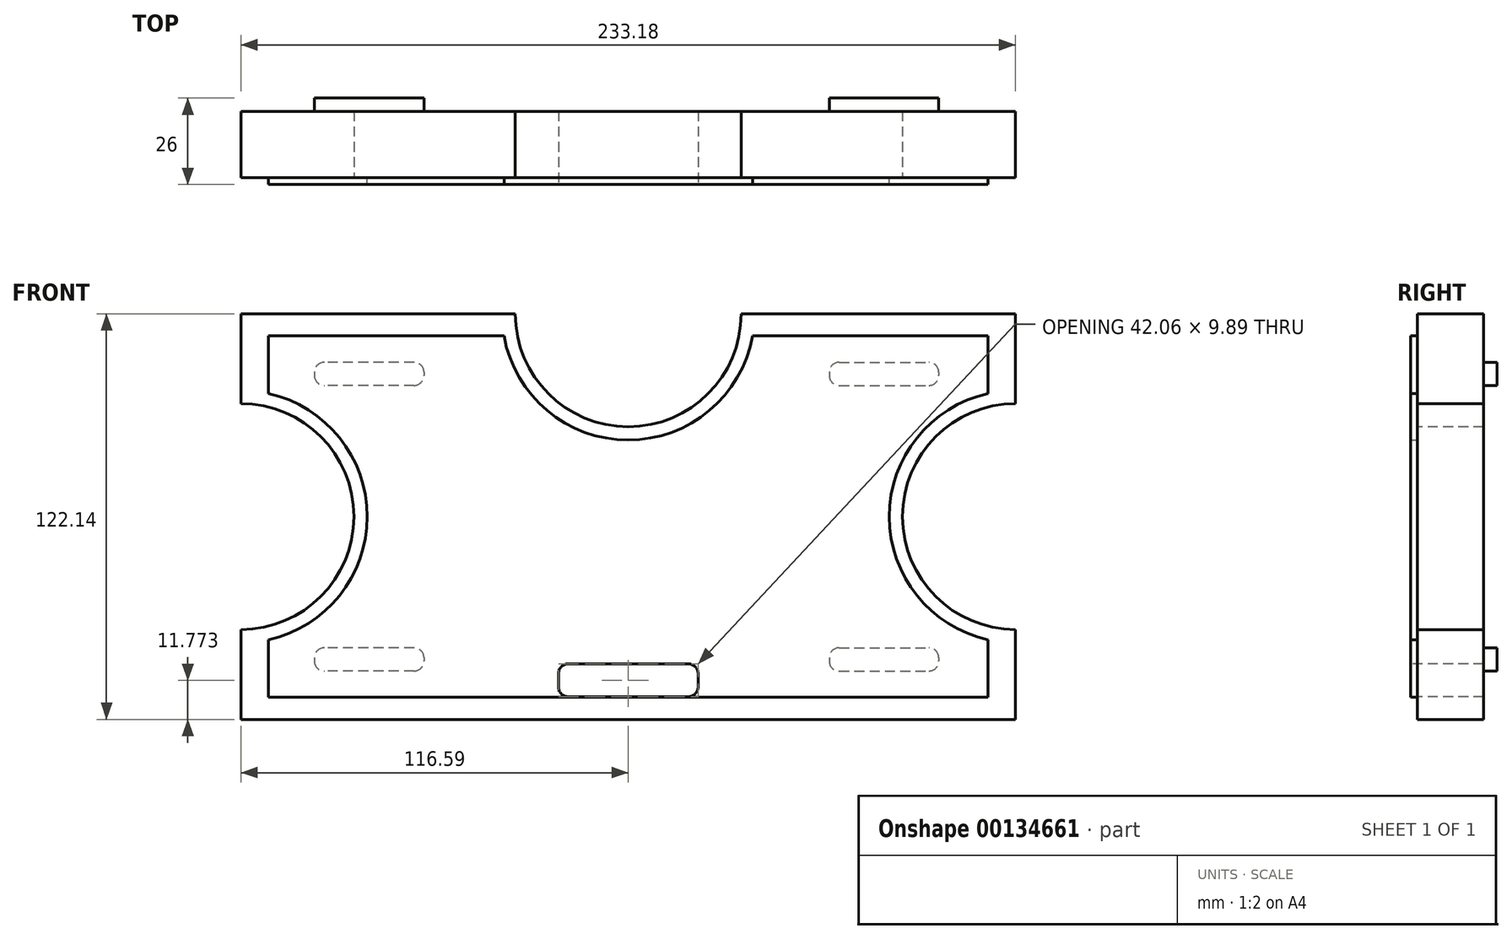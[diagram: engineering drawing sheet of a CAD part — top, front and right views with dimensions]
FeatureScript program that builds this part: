
annotation { "Feature Type Name" : "Feature", "Feature Type Description" : "" }
export const myFeature = defineFeature(function(context is Context, id is Id, definition is map)
    precondition{}
    {
        {
            var Q0;
            Q0=qCreatedBy(makeId("Front.planeOp"),FACE);
            var sketch = newSketch(context, id + "F0", { "sketchPlane" : qUnion([Q0])});
            skLineSegment(sketch, "E0.bottom", {"start": v(116.6, 61.07) * mm, "end": v(34, 61.07) * mm});
            skLineSegment(sketch, "E0.top", {"start": v(116.6, -61.07) * mm, "end": v(34, -61.07) * mm});
            skLineSegment(sketch, "E0.left", {"start": v(116.6, 61.07) * mm, "end": v(116.6, 34) * mm});
            skLineSegment(sketch, "E0.right", {"start": v(-116.6, 61.07) * mm, "end": v(-116.6, 34) * mm});
            skPoint(sketch, "E0.middle", {"position": v(0, 0) * mm});
            skArc(sketch, "E1", {"start": v(-34, 61.07) * mm, "mid": v(0, 27.07) * mm, "end": v(34, 61.07) * mm});
            skArc(sketch, "E2", {"start": v(116.6, 34) * mm, "mid": v(82.6, 0) * mm, "end": v(116.6, -34) * mm});
            skArc(sketch, "E3", {"start": v(-116.6, -34) * mm, "mid": v(-82.6, 0) * mm, "end": v(-116.6, 34) * mm});
            skLineSegment(sketch, "E4.trimOffspring", {"start": v(-116.6, -34) * mm, "end": v(-116.6, -61.07) * mm});
            skLineSegment(sketch, "E5.trimOffspring", {"start": v(34, -61.07) * mm, "end": v(-116.6, -61.07) * mm});
            skLineSegment(sketch, "E6.trimOffspring", {"start": v(-34, 61.07) * mm, "end": v(-116.6, 61.07) * mm});
            skLineSegment(sketch, "E7.trimOffspring", {"start": v(116.6, -34) * mm, "end": v(116.6, -61.07) * mm});
            skLineSegment(sketch, "E8.bottom", {"start": v(18.03, -44.35) * mm, "end": v(-18.03, -44.35) * mm});
            skLineSegment(sketch, "E8.top", {"start": v(18.03, -54.24) * mm, "end": v(-18.03, -54.24) * mm});
            skLineSegment(sketch, "E8.left", {"start": v(21.03, -47.35) * mm, "end": v(21.03, -51.24) * mm});
            skLineSegment(sketch, "E8.right", {"start": v(-21.03, -47.35) * mm, "end": v(-21.03, -51.24) * mm});
            skPoint(sketch, "E8.middle", {"position": v(0, -49.3) * mm});
            skPoint(sketch, "E9.visualSharp", {"position": v(-21.03, -44.35) * mm});
            skArc(sketch, "E9.filletArc", {"start": v(-18.03, -44.35) * mm, "mid": v(-20.15, -45.23) * mm, "end": v(-21.03, -47.35) * mm});
            skPoint(sketch, "E10.visualSharp", {"position": v(21.03, -44.35) * mm});
            skArc(sketch, "E10.filletArc", {"start": v(21.03, -47.35) * mm, "mid": v(20.15, -45.23) * mm, "end": v(18.03, -44.35) * mm});
            skPoint(sketch, "E11.visualSharp", {"position": v(21.03, -54.24) * mm});
            skArc(sketch, "E11.filletArc", {"start": v(18.03, -54.24) * mm, "mid": v(20.15, -53.36) * mm, "end": v(21.03, -51.24) * mm});
            skPoint(sketch, "E12.visualSharp", {"position": v(-21.03, -54.24) * mm});
            skArc(sketch, "E12.filletArc", {"start": v(-21.03, -51.24) * mm, "mid": v(-20.15, -53.36) * mm, "end": v(-18.03, -54.24) * mm});
            skSolve(sketch);
        }
        {
            var Q0;
            Q0=makeQuery(id+"F0.imprint","IMPRINT",FACE,{"disambiguationData":[TD([[makeQuery(id+"F0.imprint","IMPRINT",EDGE,{"derivedFrom":sQuery(id+"F0.wireOp",EDGE,"E0.bottom")}),1.0]])]});
            extrude(context, id + "F1", {"entities" : qUnion([Q0]), "oppositeDirection" : true, "depth" : 20 * mm});
        }
        {
            var Q0;
            Q0=makeQuery(id+"F1.opExtrude","CAP_FACE",FACE,{"disambiguationData":[OSD([sQuery(id+"F0.wireOp",EDGE,"E0.bottom"),sQuery(id+"F0.wireOp",EDGE,"E0.top"),sQuery(id+"F0.wireOp",EDGE,"E0.left"),sQuery(id+"F0.wireOp",EDGE,"E0.right"),sQuery(id+"F0.wireOp",EDGE,"E1"),sQuery(id+"F0.wireOp",EDGE,"E2"),sQuery(id+"F0.wireOp",EDGE,"E3"),sQuery(id+"F0.wireOp",EDGE,"E4.trimOffspring"),sQuery(id+"F0.wireOp",EDGE,"E5.trimOffspring"),sQuery(id+"F0.wireOp",EDGE,"E6.trimOffspring"),sQuery(id+"F0.wireOp",EDGE,"E7.trimOffspring"),sQuery(id+"F0.wireOp",EDGE,"E8.bottom"),sQuery(id+"F0.wireOp",EDGE,"E8.top"),sQuery(id+"F0.wireOp",EDGE,"E8.left"),sQuery(id+"F0.wireOp",EDGE,"E8.right")])],"isStart":true});
            var sketch = newSketch(context, id + "F2", { "sketchPlane" : qUnion([Q0])});
            skLineSegment(sketch, "E13.bottom", {"start": v(108.3, 54.4) * mm, "end": v(37.41, 54.4) * mm});
            skLineSegment(sketch, "E13.top", {"start": v(108.3, -54.4) * mm, "end": v(-108.3, -54.4) * mm});
            skLineSegment(sketch, "E13.left", {"start": v(108.3, 54.4) * mm, "end": v(108.3, 37.08) * mm});
            skLineSegment(sketch, "E13.right", {"start": v(-108.3, 54.4) * mm, "end": v(-108.3, 37.08) * mm});
            skPoint(sketch, "E13.middle", {"position": v(0, 0) * mm});
            skArc(sketch, "E14", {"start": v(-108.3, -37.08) * mm, "mid": v(-78.6, 0) * mm, "end": v(-108.3, 37.08) * mm});
            skArc(sketch, "E15", {"start": v(108.3, 37.08) * mm, "mid": v(78.6, 0) * mm, "end": v(108.3, -37.08) * mm});
            skLineSegment(sketch, "E16.trimOffspring", {"start": v(-108.3, -37.08) * mm, "end": v(-108.3, -54.4) * mm});
            skLineSegment(sketch, "E17.trimOffspring", {"start": v(108.3, -37.08) * mm, "end": v(108.3, -54.4) * mm});
            skArc(sketch, "E18", {"start": v(-37.41, 54.4) * mm, "mid": v(0, 23.07) * mm, "end": v(37.41, 54.4) * mm});
            skLineSegment(sketch, "E19.trimOffspring", {"start": v(-37.41, 54.4) * mm, "end": v(-108.3, 54.4) * mm});
            skSolve(sketch);
        }
        {
            var Q0;
            Q0=makeQuery(id+"F2.imprint","IMPRINT",FACE,{"disambiguationData":[TD([[makeQuery(id+"F2.imprint","IMPRINT",EDGE,{"derivedFrom":sQuery(id+"F2.wireOp",EDGE,"E13.bottom")}),1.0]])]});
            extrude(context, id + "F3", {"entities" : qUnion([Q0]), "operationType" : NewBodyOperationType.ADD, "depth" : 2 * mm});
        }
        {
            var Q0;
            Q0=makeQuery(id+"F1.opExtrude","CAP_FACE",FACE,{"disambiguationData":[OSD([sQuery(id+"F0.wireOp",EDGE,"E0.bottom"),sQuery(id+"F0.wireOp",EDGE,"E0.top"),sQuery(id+"F0.wireOp",EDGE,"E0.left"),sQuery(id+"F0.wireOp",EDGE,"E0.right"),sQuery(id+"F0.wireOp",EDGE,"E1"),sQuery(id+"F0.wireOp",EDGE,"E2"),sQuery(id+"F0.wireOp",EDGE,"E3"),sQuery(id+"F0.wireOp",EDGE,"E4.trimOffspring"),sQuery(id+"F0.wireOp",EDGE,"E5.trimOffspring"),sQuery(id+"F0.wireOp",EDGE,"E6.trimOffspring"),sQuery(id+"F0.wireOp",EDGE,"E7.trimOffspring"),sQuery(id+"F0.wireOp",EDGE,"E8.bottom"),sQuery(id+"F0.wireOp",EDGE,"E8.top"),sQuery(id+"F0.wireOp",EDGE,"E8.left"),sQuery(id+"F0.wireOp",EDGE,"E8.right")])],"isStart":false});
            var sketch = newSketch(context, id + "F4", { "sketchPlane" : qUnion([Q0])});
            skLineSegment(sketch, "E20.bottom", {"start": v(-63.5, 46.5) * mm, "end": v(-90.5, 46.5) * mm});
            skLineSegment(sketch, "E20.top", {"start": v(-63.5, 39.5) * mm, "end": v(-90.5, 39.5) * mm});
            skLineSegment(sketch, "E20.left", {"start": v(-60.5, 43.5) * mm, "end": v(-60.5, 42.5) * mm});
            skLineSegment(sketch, "E20.right", {"start": v(-93.5, 43.5) * mm, "end": v(-93.5, 42.5) * mm});
            skPoint(sketch, "E20.middle", {"position": v(-77, 43) * mm});
            skLineSegment(sketch, "E21.bottom", {"start": v(-63.5, -39.5) * mm, "end": v(-90.5, -39.5) * mm});
            skLineSegment(sketch, "E21.top", {"start": v(-63.5, -46.5) * mm, "end": v(-90.5, -46.5) * mm});
            skLineSegment(sketch, "E21.left", {"start": v(-60.5, -42.5) * mm, "end": v(-60.5, -43.5) * mm});
            skLineSegment(sketch, "E21.right", {"start": v(-93.5, -42.5) * mm, "end": v(-93.5, -43.5) * mm});
            skPoint(sketch, "E21.middle", {"position": v(-77, -43) * mm});
            skLineSegment(sketch, "E22.bottom", {"start": v(64.5, 46.5) * mm, "end": v(91.5, 46.5) * mm});
            skLineSegment(sketch, "E22.top", {"start": v(64.5, 39.5) * mm, "end": v(91.5, 39.5) * mm});
            skLineSegment(sketch, "E22.left", {"start": v(61.5, 43.5) * mm, "end": v(61.5, 42.5) * mm});
            skLineSegment(sketch, "E22.right", {"start": v(94.5, 43.5) * mm, "end": v(94.5, 42.5) * mm});
            skPoint(sketch, "E22.middle", {"position": v(78, 43) * mm});
            skLineSegment(sketch, "E23.bottom", {"start": v(64.5, -39.5) * mm, "end": v(91.5, -39.5) * mm});
            skLineSegment(sketch, "E23.top", {"start": v(64.5, -46.5) * mm, "end": v(91.5, -46.5) * mm});
            skLineSegment(sketch, "E23.left", {"start": v(61.5, -42.5) * mm, "end": v(61.5, -43.5) * mm});
            skLineSegment(sketch, "E23.right", {"start": v(94.5, -42.5) * mm, "end": v(94.5, -43.5) * mm});
            skPoint(sketch, "E23.middle", {"position": v(78, -43) * mm});
            skPoint(sketch, "E24.visualSharp", {"position": v(-93.5, 46.5) * mm});
            skArc(sketch, "E24.filletArc", {"start": v(-90.5, 46.5) * mm, "mid": v(-92.62, 45.62) * mm, "end": v(-93.5, 43.5) * mm});
            skPoint(sketch, "E25.visualSharp", {"position": v(-93.5, 39.5) * mm});
            skArc(sketch, "E25.filletArc", {"start": v(-93.5, 42.5) * mm, "mid": v(-92.62, 40.38) * mm, "end": v(-90.5, 39.5) * mm});
            skPoint(sketch, "E26.visualSharp", {"position": v(-60.5, 46.5) * mm});
            skArc(sketch, "E26.filletArc", {"start": v(-60.5, 43.5) * mm, "mid": v(-61.38, 45.62) * mm, "end": v(-63.5, 46.5) * mm});
            skPoint(sketch, "E27.visualSharp", {"position": v(-60.5, 39.5) * mm});
            skArc(sketch, "E27.filletArc", {"start": v(-63.5, 39.5) * mm, "mid": v(-61.38, 40.38) * mm, "end": v(-60.5, 42.5) * mm});
            skPoint(sketch, "E28.visualSharp", {"position": v(61.5, 46.5) * mm});
            skArc(sketch, "E28.filletArc", {"start": v(64.5, 46.5) * mm, "mid": v(62.38, 45.62) * mm, "end": v(61.5, 43.5) * mm});
            skPoint(sketch, "E29.visualSharp", {"position": v(94.5, 46.5) * mm});
            skArc(sketch, "E29.filletArc", {"start": v(94.5, 43.5) * mm, "mid": v(93.62, 45.62) * mm, "end": v(91.5, 46.5) * mm});
            skPoint(sketch, "E30.visualSharp", {"position": v(61.5, 39.5) * mm});
            skArc(sketch, "E30.filletArc", {"start": v(61.5, 42.5) * mm, "mid": v(62.38, 40.38) * mm, "end": v(64.5, 39.5) * mm});
            skPoint(sketch, "E31.visualSharp", {"position": v(94.5, 39.5) * mm});
            skArc(sketch, "E31.filletArc", {"start": v(91.5, 39.5) * mm, "mid": v(93.62, 40.38) * mm, "end": v(94.5, 42.5) * mm});
            skPoint(sketch, "E32.visualSharp", {"position": v(61.5, -39.5) * mm});
            skArc(sketch, "E32.filletArc", {"start": v(64.5, -39.5) * mm, "mid": v(62.38, -40.38) * mm, "end": v(61.5, -42.5) * mm});
            skPoint(sketch, "E33.visualSharp", {"position": v(61.5, -46.5) * mm});
            skArc(sketch, "E33.filletArc", {"start": v(61.5, -43.5) * mm, "mid": v(62.38, -45.62) * mm, "end": v(64.5, -46.5) * mm});
            skPoint(sketch, "E34.visualSharp", {"position": v(94.5, -39.5) * mm});
            skArc(sketch, "E34.filletArc", {"start": v(94.5, -42.5) * mm, "mid": v(93.62, -40.38) * mm, "end": v(91.5, -39.5) * mm});
            skPoint(sketch, "E35.visualSharp", {"position": v(94.5, -46.5) * mm});
            skArc(sketch, "E35.filletArc", {"start": v(91.5, -46.5) * mm, "mid": v(93.62, -45.62) * mm, "end": v(94.5, -43.5) * mm});
            skPoint(sketch, "E36.visualSharp", {"position": v(-60.5, -39.5) * mm});
            skArc(sketch, "E36.filletArc", {"start": v(-60.5, -42.5) * mm, "mid": v(-61.38, -40.38) * mm, "end": v(-63.5, -39.5) * mm});
            skPoint(sketch, "E37.visualSharp", {"position": v(-93.5, -39.5) * mm});
            skArc(sketch, "E37.filletArc", {"start": v(-90.5, -39.5) * mm, "mid": v(-92.62, -40.38) * mm, "end": v(-93.5, -42.5) * mm});
            skPoint(sketch, "E38.visualSharp", {"position": v(-93.5, -46.5) * mm});
            skArc(sketch, "E38.filletArc", {"start": v(-93.5, -43.5) * mm, "mid": v(-92.62, -45.62) * mm, "end": v(-90.5, -46.5) * mm});
            skPoint(sketch, "E39.visualSharp", {"position": v(-60.5, -46.5) * mm});
            skArc(sketch, "E39.filletArc", {"start": v(-63.5, -46.5) * mm, "mid": v(-61.38, -45.62) * mm, "end": v(-60.5, -43.5) * mm});
            skSolve(sketch);
        }
        {
            var Q0;
            Q0=makeQuery(id+"F4.imprint","IMPRINT",FACE,{"disambiguationData":[TD([[makeQuery(id+"F4.imprint","IMPRINT",EDGE,{"derivedFrom":sQuery(id+"F4.wireOp",EDGE,"E20.bottom")}),1.0]])]});
            extrude(context, id + "F5", {"entities" : qUnion([Q0]), "operationType" : NewBodyOperationType.ADD, "depth" : 4 * mm});
        }
        {
            var Q0;
            Q0 = qSketchRegion(id + "F4", true);
            extrude(context, id + "F6", {"entities" : qUnion([Q0]), "operationType" : NewBodyOperationType.ADD, "depth" : 4 * mm});
        }
    });
